# Revit family: BathMixer-(Built-in)-Vitra-İstanbulSeries-A48015
name_source: partatom
category: Plumbing Fixtures
revit_build: Autodesk Revit 2017 (Build: 20160225_1515(x64)
units: mm (PartAtom-declared; Revit-internal decimal feet)

## family parameters
Cut with Voids When Loaded = No
Host = Face
OmniClass Number = 23.45.55.17
OmniClass Title = Mixing Faucets
Part Type = Normal
Room Calculation Point = No
Round Connector Dimension = Use Diameter
Shared = Yes

## types (1)
- BathMixer-(Built-in)-Vitra-İstanbulSeries-A48015
    Article No. (default) = A48015
    BIMobject category = Bath/Shower Mixer
    Brand = VitrA
    CW Connection = Yes
    Coating Material = Chrome
    Color = Chrome
    Connection Diameter (mm) = 15 mm  [stored 0.0492126 ft]
    Default Elevation = 850 mm  [stored 2.78871 ft]
    Description = Istanbul the hand shower- hand shower with anti-lime function Easy Clean
    Design country = Turkey
    Flow Rate(L/min. - 3 bar) = 8 L/min.
    HW Connection = Yes
    Hot Water Supply (max.) = 80 °C
    Hot Water temperature, factory set to = 38 °C
    IFC Classification = Sanitary Terminal
    Main Material = Metal
    Manufacturer = VitrA
    Manufacturer name = VitrA
    Masterformat 2014 Code = 22 40 00
    Masterformat 2014 Description = Plumbing Fixtures
    Min. flow pressure of = 0.5 bar
    Model = A48015
    Mounting type = Wall Mounted
    NBS Referans Code = 45-35-70/315
    NBS Referans Description = Water supply fittings for baths
    Nominal Depth (mm) = 70 mm
    Nominal Height (mm) = 510 mm  [stored 1.67323 ft]
    Nominal Width (mm) = 100 mm  [stored 0.328084 ft]
    Number Of Connections = 1
    OmniClass Code = 23.45.55.17
    OmniClass Description = Mixing Faucets
    Primary Material = <By Category>
    Product SKU = A48015
    Product Type = Built-in bath mixer
    Product certification = https://www.vitraglobal.com
    Product family = İstanbul
    Product group = Bath Mixer
    Product url = https://www.vitra.com.tr
    Range of Hot Water Supply = 5 - 65 °C
    Range of flow pressure = 1 - 5 bar
    Technical description = https://www.vitra.com.tr
    Test Pressure = 16 bar
    URL = https://vitraglobal.com
    Uniclass 1.4 Code = L725111
    Uniclass 1.4 Description = Mixer taps
    Uniclass 2.0 Code = Pr_40_20_87_09
    Uniclass 2.0 Description = Bath taps
    Uniclass 2015 Code = Pr_40_20_87_09
    Uniclass 2015 Name = Bath taps
    Uniformat II Code = 22 40 00
    Uniformat II Description = Plumbing Fixture
    Vent Connection = No
    Warranty Period (Year) = 5 Years
    Waste Connection = No
    Weight Net (kg) = 1.15
    Youtube = https://www.youtube.com

note: [stored X ft] marks values corroborated as IEEE doubles in the binary element streams (Revit-internal decimal feet)

## geometry (parser evidence)
native form markers: Sweep x2
no freeform markers — native parametric forms only
